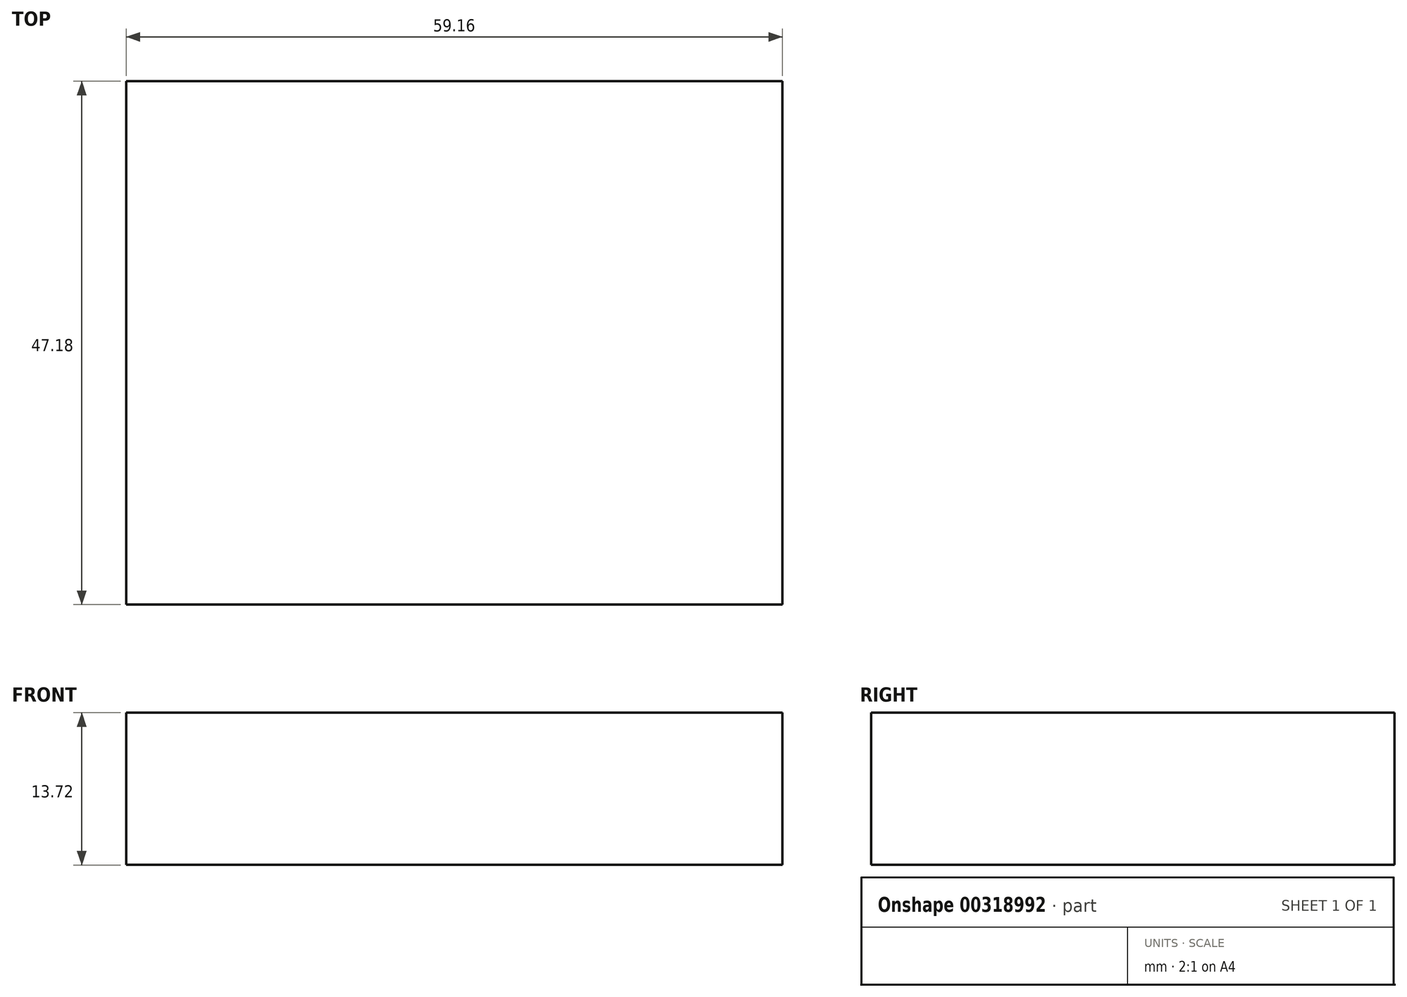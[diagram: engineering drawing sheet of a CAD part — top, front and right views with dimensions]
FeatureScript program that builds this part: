
annotation { "Feature Type Name" : "Feature", "Feature Type Description" : "" }
export const myFeature = defineFeature(function(context is Context, id is Id, definition is map)
    precondition{}
    {
        {
            var Q0;
            Q0=qCreatedBy(makeId("Top.planeOp"),FACE);
            var sketch = newSketch(context, id + "F0", { "sketchPlane" : qUnion([Q0])});
            skLineSegment(sketch, "E0.bottom", {"start": v(0, 0) * mm, "end": v(59.16, 0) * mm});
            skLineSegment(sketch, "E0.top", {"start": v(0, -47.18) * mm, "end": v(59.16, -47.18) * mm});
            skLineSegment(sketch, "E0.left", {"start": v(0, 0) * mm, "end": v(0, -47.18) * mm});
            skLineSegment(sketch, "E0.right", {"start": v(59.16, 0) * mm, "end": v(59.16, -47.18) * mm});
            skSolve(sketch);
        }
        {
            var Q0;
            Q0 = qSketchRegion(id + "F0", true);
            extrude(context, id + "F1", {"entities" : qUnion([Q0]), "oppositeDirection" : true, "depth" : 13.72 * mm});
        }
    });
